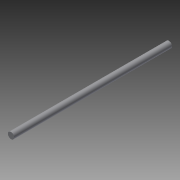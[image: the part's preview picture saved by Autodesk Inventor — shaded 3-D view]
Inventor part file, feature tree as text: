
AUTODESK INVENTOR PART (.ipt)
format: ipt  version: 2014 (Build 180170000, 170)  size: 65,536 bytes
history: native  units: mm
features: extrude x1, sketch x1
ambient origin geometry x8: Origin, YZ Plane, XZ Plane, XY Plane, X Axis, Y Axis, Z Axis, Center Point
bodies: Solid1 (feature_tree)
feature tree (2):
  extrude  "Extrusion1"  Depth=125.0mm TaperAngle=0.0deg
  sketch  "Sketch1"  dims[d0=5.0mm d1=125.0mm d2=0.0mm]
